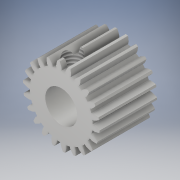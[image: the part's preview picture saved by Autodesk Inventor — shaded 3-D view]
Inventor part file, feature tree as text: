
AUTODESK INVENTOR PART (.ipt)
format: ipt  version: 2017 (Build 210142000, 142)  size: 564,736 bytes
history: native  units: in
note: dims shown in document units (in); Inventor stores cm internally (conversion verified against a paired STEP export)
features: sketch x6, extrude x5, other x2, plane x2, pattern_circular x1, thread x1
ambient origin geometry x8: Origin, YZ Plane, XZ Plane, XY Plane, X Axis, Y Axis, Z Axis, Center Point
bodies: Solid1 (feature_tree)
feature tree (17):
  sketch  "Sketch2"  dims[d0=0.4331in d1=0.1374in]
  extrude  "Extrusion1"  Depth=0.1374in
  extrude  "Extrusion3"  Depth=0.0394in
  pattern_circular  "Circular Pattern1"  [2 undecoded]
  extrude  "Extrusion12"  Depth=0.3937in TaperAngle=360.0deg
  extrude  "Extrusion19"  Depth=0.3937in
  other  "Work Point1"
  plane  "Work Plane16"
  extrude  "Extrusion20"  Depth=0.3937in
  thread  "Thread1"  [1 undecoded]
  plane  "Work Plane17"
  sketch  "Sketch4"  dims[d6=0.0741in d7=0.0394in]
  sketch  "Sketch5"  dims[d8=0.0347in]
  sketch  "Sketch24"  dims[d9=0.0281in]
  sketch  "Sketch47"  dims[d10=0.5906in]
  other  "Work Axis5"
  sketch  "Sketch48"  dims[d12=0.3543in d13=0.0in d16=0.1969in d17=0.0in d18=8.6614in d19=360.0deg d61=0.0472in d62=0.1213in d64=0.0098in d121=0.4724in d122=0.9449in d123=0.3937in d124=0.0in d183=0.1969in d184=0.3937in d185=0.0in d186=0.1102in d188=0.3937in d189=0.0in d190=0.3937in d191=0.0in d192=0.0866in]
note: 3 required parameter values undecoded (feature->parameter linkage not recoverable at this tier; creation-order binding heuristic only, values carry confidence <= 0.55)
